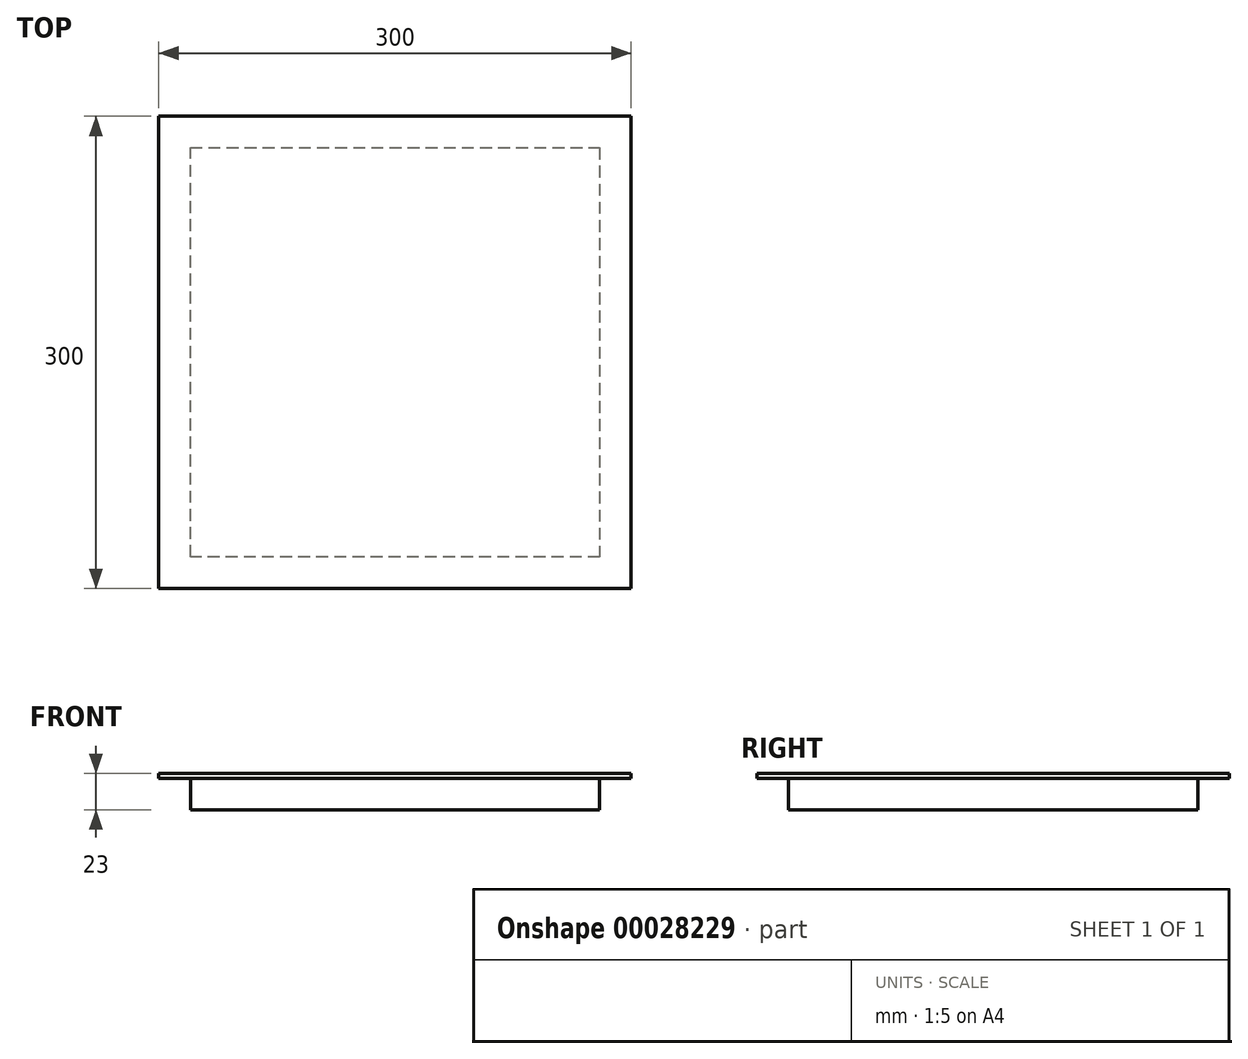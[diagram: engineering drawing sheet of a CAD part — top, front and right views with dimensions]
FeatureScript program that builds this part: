
annotation { "Feature Type Name" : "Feature", "Feature Type Description" : "" }
export const myFeature = defineFeature(function(context is Context, id is Id, definition is map)
    precondition{}
    {
        {
            var Q0;
            Q0=qCreatedBy(makeId("Top.planeOp"),FACE);
            var sketch = newSketch(context, id + "F0", { "sketchPlane" : qUnion([Q0])});
            skLineSegment(sketch, "E0.rect.bottom", {"start": v(-150, 150) * mm, "end": v(150, 150) * mm});
            skLineSegment(sketch, "E0.rect.top", {"start": v(-150, -150) * mm, "end": v(150, -150) * mm});
            skLineSegment(sketch, "E0.rect.left", {"start": v(-150, 150) * mm, "end": v(-150, -150) * mm});
            skLineSegment(sketch, "E0.rect.right", {"start": v(150, 150) * mm, "end": v(150, -150) * mm});
            skPoint(sketch, "E0.rect.middle", {"position": v(0, 0) * mm});
            skSolve(sketch);
        }
        {
            var Q0;
            Q0 = qSketchRegion(id + "F0", true);
            extrude(context, id + "F1", {"entities" : qUnion([Q0]), "depth" : 3 * mm});
        }
        {
            var Q0;
            Q0=makeQuery(id+"F1.opExtrude","CAP_FACE",FACE,{"disambiguationData":[OSD([sQuery(id+"F0.wireOp",EDGE,"E0.rect.bottom"),sQuery(id+"F0.wireOp",EDGE,"E0.rect.top"),sQuery(id+"F0.wireOp",EDGE,"E0.rect.left"),sQuery(id+"F0.wireOp",EDGE,"E0.rect.right")])],"isStart":true});
            var sketch = newSketch(context, id + "F2", { "sketchPlane" : qUnion([Q0])});
            skLineSegment(sketch, "E1.0.0", {"start": v(-150, -150) * mm, "end": v(150, -150) * mm, "construction": true});
            skLineSegment(sketch, "E1.0.1", {"start": v(150, -150) * mm, "end": v(150, 150) * mm, "construction": true});
            skLineSegment(sketch, "E1.0.2", {"start": v(150, 150) * mm, "end": v(-150, 150) * mm, "construction": true});
            skLineSegment(sketch, "E1.0.3", {"start": v(-150, 150) * mm, "end": v(-150, -150) * mm, "construction": true});
            skLineSegment(sketch, "E2.0", {"start": v(-130, 130) * mm, "end": v(-130, -130) * mm});
            skLineSegment(sketch, "E2.1", {"start": v(130, 130) * mm, "end": v(-130, 130) * mm});
            skLineSegment(sketch, "E2.2", {"start": v(130, -130) * mm, "end": v(130, 130) * mm});
            skLineSegment(sketch, "E2.3", {"start": v(-130, -130) * mm, "end": v(130, -130) * mm});
            skSolve(sketch);
        }
        {
            var Q0;
            Q0 = qSketchRegion(id + "F2", true);
            extrude(context, id + "F3", {"entities" : qUnion([Q0]), "depth" : 20 * mm});
        }
    });
